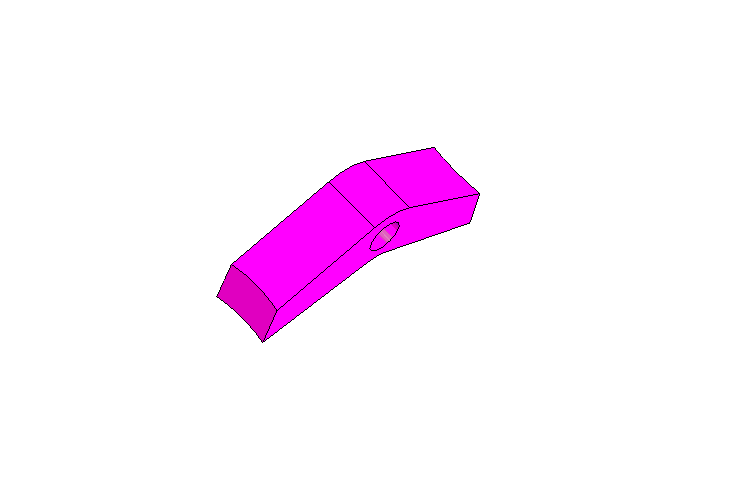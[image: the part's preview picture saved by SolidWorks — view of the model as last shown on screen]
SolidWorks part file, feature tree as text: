
SOLIDWORKS PART (.sldprt)
format: sldprt  version: not decoded by parser v0  size: 383,488 bytes
history: native  units: mm
features: plane x10, sketch x10, material x1, extrude x1, cut_extrude x1, mirror x1 + 1 further entry (+9 scaffold rows collapsed)
feature tree (34):
  "Annotations"  RD1=15.75deg
  scaffold x9  (default folders/planes/origin — collapsed)
  material  "Matériau <non spécifié>"
  plane  "Plan de face"
  plane  "Plan de dessus"
  plane  "Plan de droite"
  sketch  "Esquisse1"  dims[c1.D1=625.0mm c1.D2=460.0mm c1.D3=545.0mm c1.D4=27.0mm c1.D5=500.0mm c1.D6=445.0mm c1.D7=670.0mm c2.D1=622.0mm c2.D2=670.0mm c2.D3=545.0mm c2.D4=460.0mm c2.D5=445.0mm c2.D6=495.0mm c2.D7=535.0mm c2.D8=27.0mm c2.D9=8.0mm c2.D10=155.0mm c2.D11=400.0mm c2.D12=~545.374305mm c3.D12=56.0deg]
  plane  "Plan1"
  plane  "Plan2"
  sketch  "Esquisse2"  dims[c1.D2=75.0mm c1.D1=102.0mm c1.D3=103.0mm c2.D1=102.0mm c2.D4=~138.45102mm c3.D4=45.0deg]
  sketch  "Esquisse3"  dims[D1=112.0mm]
  plane  "Plan3"
  sketch  "Esquisse4"  dims[D1=500.0mm]
  sketch  "Esquisse14"  dims[c1.D1=6.5mm c1.D2=14.0mm c1.D5=12.0mm c1.D6=8.0mm c2.D2=150.0mm c2.D3=8.5mm c2.D4=6.0mm c2.D7=~10.779001mm c3.D7=146.0deg c3.D8=~18.442278mm c4.D8=130.0deg]
  extrude  "Extrusion1"  Depth=14mm
  sketch  "Esquisse15"  dims[D1=8.0mm]
  cut_extrude  "Enlèv. mat.-Extru.1"  Depth=11mm
  plane  "Plan4"
  plane  "Plan5"
  plane  "Plan6"
  plane  "Plan7"
  sketch  "Esquisse5"  dims[D1=16.0mm D2=27.0mm]
  sketch  "Esquisse6"  dims[D1=30.0mm D2=18.5mm]
  sketch  "Esquisse7"  dims[D1=40.0mm D2=18.0mm]
  sketch  "Esquisse8"  dims[D1=40.0mm D2=20.0mm]
  mirror  "Symétrie1"
decode coverage: 12 of 13 modeling features carry decoded parameters; 1 rows unclassified (native names shown)
note: ~ marks probable driven/reference dimensions
note: suppression state not decoded; provenance and decode notes live in map.json
